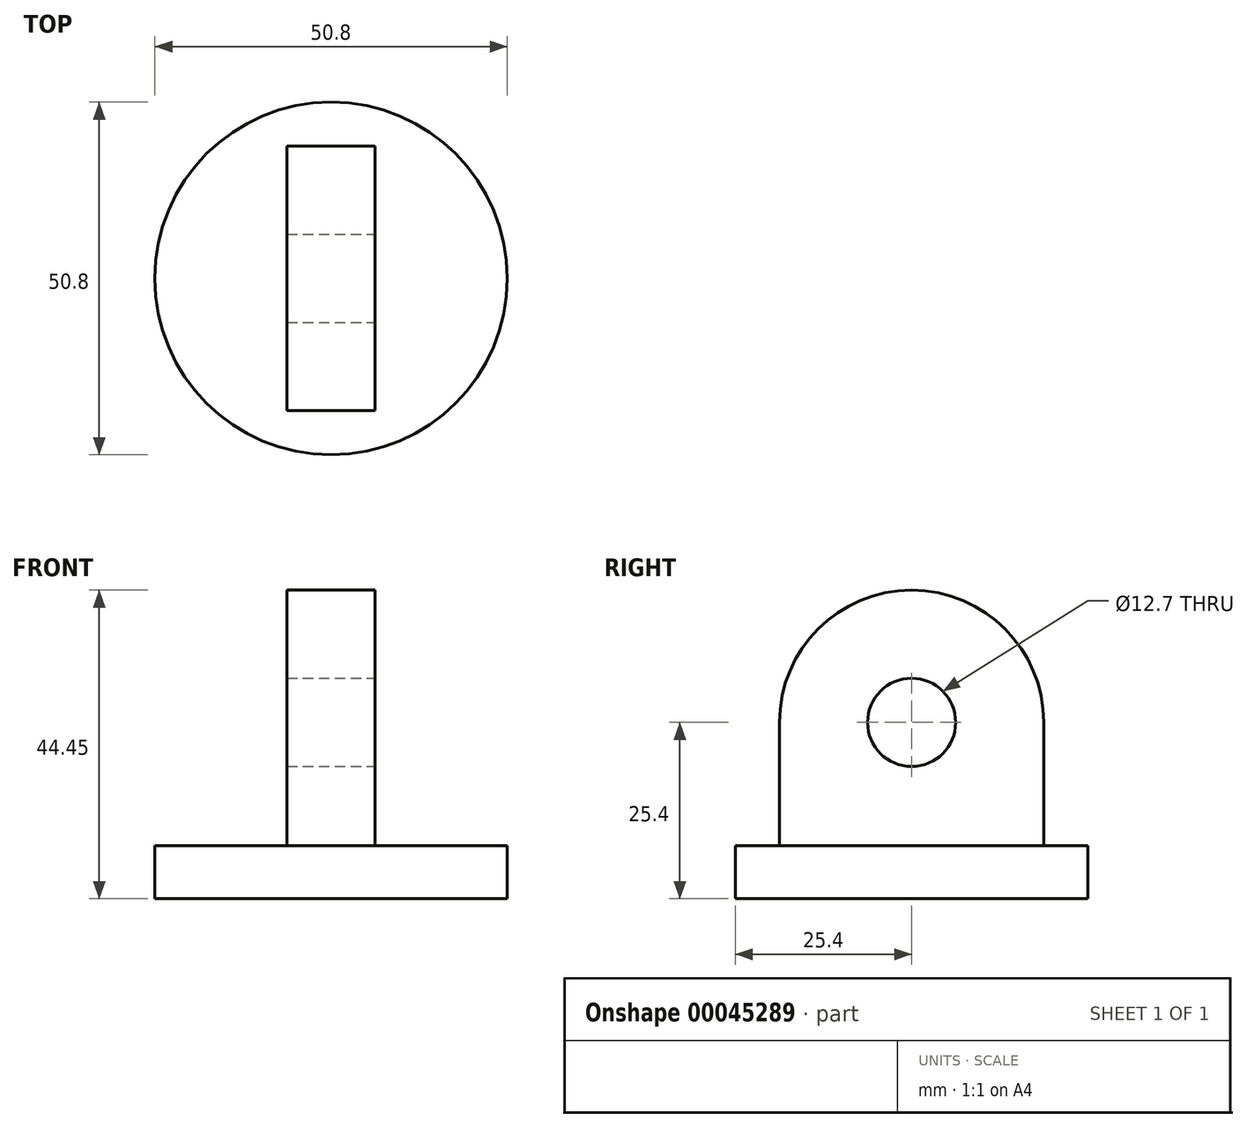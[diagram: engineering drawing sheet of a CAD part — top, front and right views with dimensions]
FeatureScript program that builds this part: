
annotation { "Feature Type Name" : "Feature", "Feature Type Description" : "" }
export const myFeature = defineFeature(function(context is Context, id is Id, definition is map)
    precondition{}
    {
        {
            var Q0;
            Q0=qCreatedBy(makeId("Top.planeOp"),FACE);
            var sketch = newSketch(context, id + "F0", { "sketchPlane" : qUnion([Q0])});
            skCircle(sketch, "E0", {"center": v(0, 0) * mm, "radius": 25.4 * mm});
            skSolve(sketch);
        }
        {
            var Q0;
            Q0=qSketchRegion(id+"F0",true);
            extrude(context, id + "F1", {"entities" : qUnion([Q0]), "endBound" : BoundingType.SYMMETRIC, "depth" : 50.8 * mm});
        }
        {
            var Q0;
            Q0=makeQuery(id+"F1.opExtrude","CAP_FACE",FACE,{"disambiguationData":[OSD([sQuery(id+"F0.wireOp",EDGE,"E0")])],"isStart":false});
            var sketch = newSketch(context, id + "F2", { "sketchPlane" : qUnion([Q0])});
            skLineSegment(sketch, "E1.left", {"start": v(-6.35, 38.1) * mm, "end": v(-6.35, -38.1) * mm});
            skLineSegment(sketch, "E1.right", {"start": v(6.35, 38.1) * mm, "end": v(6.35, -38.21) * mm});
            skLineSegment(sketch, "E2.1.0.3", {"start": v(31.75, 38.1) * mm, "end": v(31.75, -38.21) * mm});
            skLineSegment(sketch, "E3.1.0.0", {"start": v(-31.75, 38.1) * mm, "end": v(-31.75, -38.1) * mm});
            skPoint(sketch, "E4.orphan", {"position": v(19.05, -38.1) * mm});
            skLineSegment(sketch, "E5", {"start": v(-31.75, 38.1) * mm, "end": v(-6.35, 38.1) * mm});
            skLineSegment(sketch, "E6", {"start": v(6.35, 38.1) * mm, "end": v(31.75, 38.1) * mm});
            skLineSegment(sketch, "E7", {"start": v(31.75, -38.21) * mm, "end": v(6.35, -38.21) * mm});
            skLineSegment(sketch, "E8", {"start": v(-6.35, -38.1) * mm, "end": v(-31.75, -38.1) * mm});
            skSolve(sketch);
        }
        {
            var Q0;
            Q0=qSketchRegion(id+"F2",true);
            extrude(context, id + "F3", {"entities" : qUnion([Q0]), "operationType" : NewBodyOperationType.REMOVE, "oppositeDirection" : true, "depth" : 43.18 * mm});
        }
        {
            var Q0;
            Q0=qCreatedBy(makeId("Right.planeOp"),FACE);
            var sketch = newSketch(context, id + "F4", { "sketchPlane" : qUnion([Q0])});
            skCircle(sketch, "E9", {"center": v(0, 0) * mm, "radius": 6.35 * mm});
            skArc(sketch, "E10.0", {"start": v(19.05, 0) * mm, "mid": v(0, 19.05) * mm, "end": v(-19.05, 0) * mm});
            skLineSegment(sketch, "E11.bottom", {"start": v(38.1, 38.1) * mm, "end": v(-38.1, 38.1) * mm});
            skLineSegment(sketch, "E11.top", {"start": v(38.1, 0) * mm, "end": v(19.05, 0) * mm});
            skLineSegment(sketch, "E11.left", {"start": v(38.1, 38.1) * mm, "end": v(38.1, -17.78) * mm});
            skLineSegment(sketch, "E11.right", {"start": v(-38.1, 38.1) * mm, "end": v(-38.1, -17.78) * mm});
            skLineSegment(sketch, "E12", {"start": v(0, 0) * mm, "end": v(0, 66.23) * mm, "construction": true});
            skLineSegment(sketch, "E13.trimOffspring", {"start": v(-19.05, 0) * mm, "end": v(-38.1, 0) * mm});
            skLineSegment(sketch, "E14.0", {"start": v(38.1, -17.78) * mm, "end": v(19.05, -17.78) * mm});
            skLineSegment(sketch, "E15", {"start": v(-19.05, 0) * mm, "end": v(-19.05, -17.78) * mm});
            skLineSegment(sketch, "E16", {"start": v(19.05, 0) * mm, "end": v(19.05, -17.78) * mm});
            skLineSegment(sketch, "E17.trimOffspring", {"start": v(-19.05, -17.78) * mm, "end": v(-38.1, -17.78) * mm});
            skSolve(sketch);
        }
        {
            var Q0;
            Q0=qSketchRegion(id+"F4",true);
            extrude(context, id + "F5", {"entities" : qUnion([Q0]), "operationType" : NewBodyOperationType.REMOVE, "endBound" : BoundingType.SYMMETRIC, "oppositeDirection" : true, "depth" : 50.8 * mm});
        }
    });
